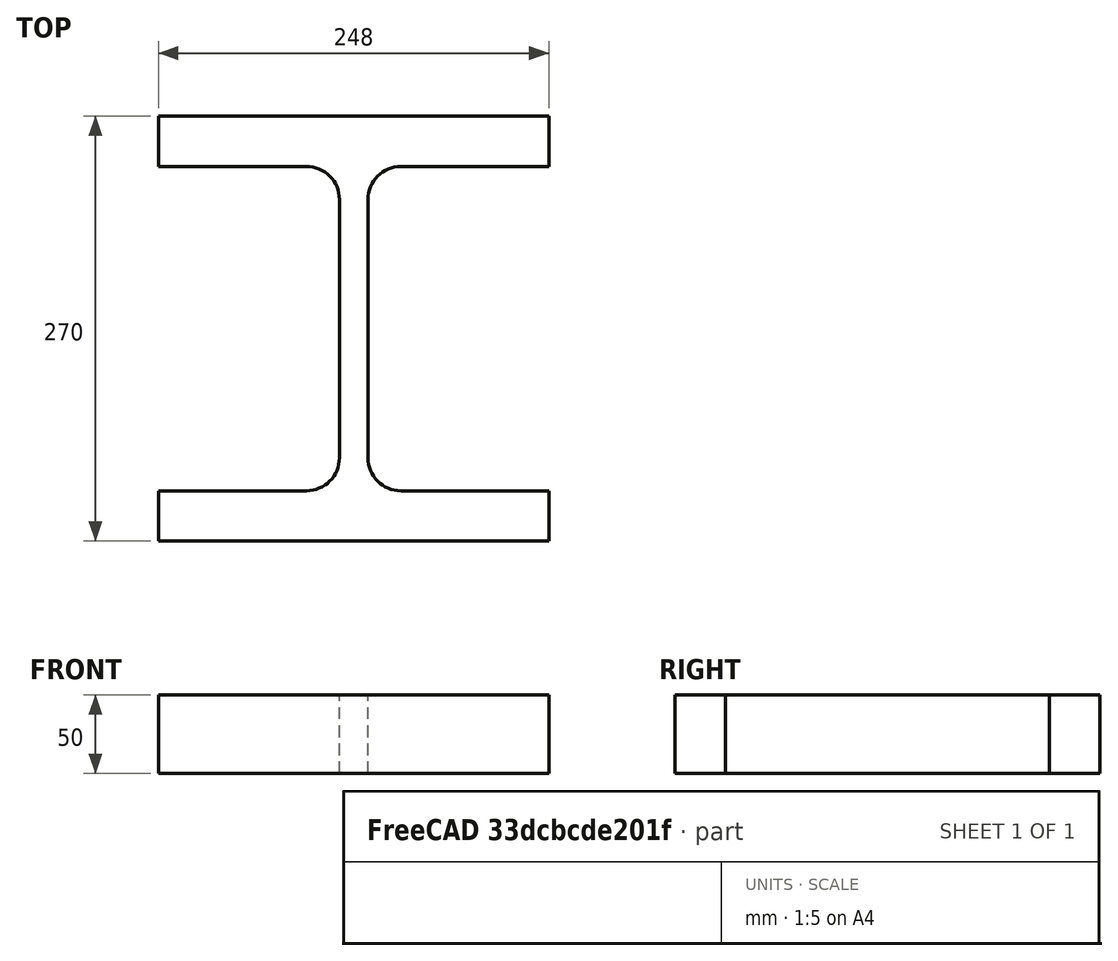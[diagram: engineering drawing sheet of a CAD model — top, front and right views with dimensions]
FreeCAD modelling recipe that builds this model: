
FCSTD DOCUMENT  (FreeCAD 0.15R4671 (Git))
Label: HE-M-Profile 240 DIN1025-4 S235JR
License: All rights reserved
LicenseURL: http://en.wikipedia.org/wiki/All_rights_reserved
objects: Sketcher::SketchObject×1, Part::Extrusion×1
note: 2 computed .brp shape members not serialized (recipe doc carries the construction recipe); baked Part::Feature solids carry a one-line shape summary decoded from their .brp

FEATURE [Sketcher::SketchObject] Sketch
  sketch-geometry (16):
    g0: LineSegment StartX=9 StartY=-82 StartZ=0 EndX=9 EndY=82 EndZ=0
    g1: LineSegment StartX=30 StartY=103 StartZ=0 EndX=124 EndY=103 EndZ=0
    g2: LineSegment StartX=124 StartY=103 StartZ=0 EndX=124 EndY=135 EndZ=0
    g3: LineSegment StartX=124 StartY=135 StartZ=0 EndX=-124 EndY=135 EndZ=0
    g4: LineSegment StartX=-124 StartY=135 StartZ=0 EndX=-124 EndY=103 EndZ=0
    g5: LineSegment StartX=-124 StartY=103 StartZ=0 EndX=-30 EndY=103 EndZ=0
    g6: LineSegment StartX=-9 StartY=82 StartZ=0 EndX=-9 EndY=-82 EndZ=0
    g7: LineSegment StartX=-30 StartY=-103 StartZ=0 EndX=-124 EndY=-103 EndZ=0
    g8: LineSegment StartX=-124 StartY=-103 StartZ=0 EndX=-124 EndY=-135 EndZ=0
    g9: LineSegment StartX=-124 StartY=-135 StartZ=0 EndX=124 EndY=-135 EndZ=0
    g10: LineSegment StartX=124 StartY=-135 StartZ=0 EndX=124 EndY=-103 EndZ=0
    g11: LineSegment StartX=124 StartY=-103 StartZ=0 EndX=30 EndY=-103 EndZ=0
    g12: ArcOfCircle CenterX=30 CenterY=82 CenterZ=0 NormalX=0 NormalY=0 NormalZ=1 Radius=21 StartAngle=1.5708 EndAngle=3.14159
    g13: ArcOfCircle CenterX=30 CenterY=-82 CenterZ=0 NormalX=0 NormalY=0 NormalZ=1 Radius=21 StartAngle=3.14159 EndAngle=4.71239
    g14: ArcOfCircle CenterX=-30 CenterY=82 CenterZ=0 NormalX=0 NormalY=0 NormalZ=1 Radius=21 StartAngle=0 EndAngle=1.5708
    g15: ArcOfCircle CenterX=-30 CenterY=-82 CenterZ=0 NormalX=0 NormalY=0 NormalZ=1 Radius=21 StartAngle=4.71239 EndAngle=6.28319
  constraints (42):
    c: Vertical(g0)
    c: Coincident(g2,g1)
    c: Vertical(g2)
    c: Coincident(g3,g2)
    c: Coincident(g4,g3)
    c: Vertical(g4)
    c: Coincident(g5,g4)
    c: Horizontal(g5)
    c: Vertical(g6)
    c: Horizontal(g7)
    c: Coincident(g8,g7)
    c: Vertical(g8)
    c: Coincident(g9,g8)
    c: Horizontal(g9)
    c: Coincident(g10,g9)
    c: Vertical(g10)
    c: Coincident(g11,g10)
    c: Horizontal(g11)
    c: Tangent(g1,g12) = 1.5708
    c: Tangent(g0,g12) = 1.5708
    c: Tangent(g0,g13) = 1.5708
    c: Tangent(g11,g13) = 1.5708
    c: Tangent(g5,g14) = 1.5708
    c: Tangent(g6,g14) = 1.5708
    c: Tangent(g6,g15) = 1.5708
    c: Tangent(g7,g15) = 1.5708
    c: Equal(g3,g9)
    c: Equal(g2,g4)
    c: Equal(g4,g8)
    c: Equal(g8,g10)
    c: Equal(g12,g14)
    c: Equal(g14,g15)
    c: Equal(g15,g13)
    c: Symmetric(g2,g3,g-2)
    c: Symmetric(g9,g8,g-2)
    c: Symmetric(g0,g6,g-2)
    c: Symmetric(g2,g9,g-1)
    c: DistanceY(g2,g9) = -270
    c: DistanceX(g3) = -248
    c: DistanceX(g0,g6) = -18
    c: DistanceY(g2) = 32
    c: Radius(g12) = 21
FEATURE [Part::Extrusion] Extrude  label="HE-M-Profile 240 DIN1025-4 S235JR"
  Base = -> Sketch
  Dir = (0,0,50)
  Solid = true
